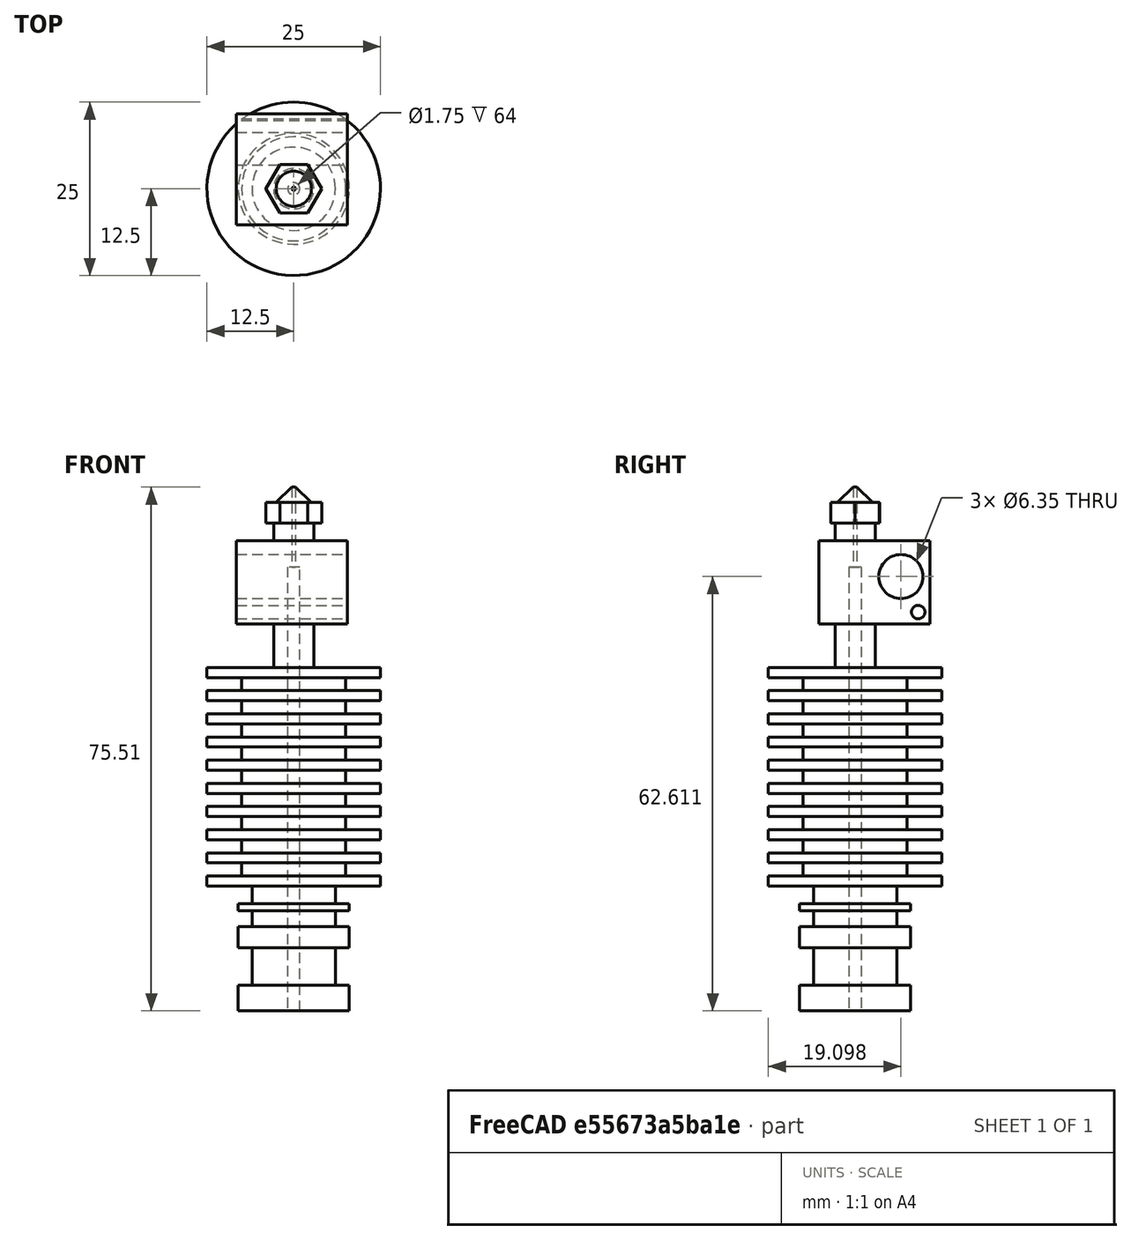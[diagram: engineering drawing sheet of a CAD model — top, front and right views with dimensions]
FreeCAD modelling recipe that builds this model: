
FCSTD DOCUMENT  (FreeCAD 0.14R3700 (Git))
Label: hotend
License: CC-BY 3.0
LicenseURL: http://creativecommons.org/licenses/by/3.0/
objects: Part::Cylinder×16, Part::Feature×3, Part::MultiFuse×3, Sketcher::SketchObject×2, PartDesign::Pocket×2, Part::Box×1, App::DocumentObjectGroup×1
note: 29 computed .brp shape members not serialized (recipe doc carries the construction recipe); baked Part::Feature solids carry a one-line shape summary decoded from their .brp

FEATURE [Part::Cylinder] Cylinder  label="Cilindro"
  Angle = 360
  Height = 3.7
  Radius = 8
FEATURE [Part::Cylinder] Cylinder001  label="Cilindro001"
  Angle = 360
  Height = 18.1
  Radius = 6
FEATURE [Part::Cylinder] Cylinder002  label="Cilindro002"
  Angle = 360
  Height = 3.06
  Placement = pos=(0,-5.16545e-06,9.1) rot=(0,0,1;0rad)
  Radius = 8
FEATURE [Part::Cylinder] Cylinder003  label="Cilindro003"
  Angle = 360
  Height = 1
  Placement = pos=(0,-5.16545e-06,14.46) rot=(0,0,1;0rad)
  Radius = 8
FEATURE [Part::Cylinder] Cylinder004  label="Cilindro004"
  Angle = 360
  Height = 1.44
  Placement = pos=(0,0,18) rot=(0,0,1;0rad)
  Radius = 12.5
FEATURE [Part::Cylinder] Cylinder005  label="Cilindro005"
  Angle = 360
  Height = 31
  Placement = pos=(0,0,18) rot=(0,0,1;0rad)
  Radius = 7.5
FEATURE [Part::Cylinder] Cylinder006  label="Cilindro006"
  Angle = 360
  Height = 1.44
  Placement = pos=(0,0,21.34) rot=(0,0,1;0rad)
  Radius = 12.5
FEATURE [Part::Cylinder] Cylinder007  label="Cilindro007"
  Angle = 360
  Height = 1.44
  Placement = pos=(0,0,24.68) rot=(0,0,1;0rad)
  Radius = 12.5
FEATURE [Part::Cylinder] Cylinder008  label="Cilindro008"
  Angle = 360
  Height = 1.44
  Placement = pos=(0,0,28.02) rot=(0,0,1;0rad)
  Radius = 12.5
FEATURE [Part::Cylinder] Cylinder009  label="Cilindro009"
  Angle = 360
  Height = 1.44
  Placement = pos=(0,0,31.36) rot=(0,0,1;0rad)
  Radius = 12.5
FEATURE [Part::Cylinder] Cylinder010  label="Cilindro010"
  Angle = 360
  Height = 1.44
  Placement = pos=(0,0,34.7) rot=(0,0,1;0rad)
  Radius = 12.5
FEATURE [Part::Cylinder] Cylinder011  label="Cilindro011"
  Angle = 360
  Height = 1.44
  Placement = pos=(0,0,38.04) rot=(0,0,1;0rad)
  Radius = 12.5
FEATURE [Part::Cylinder] Cylinder012  label="Cilindro012"
  Angle = 360
  Height = 1.44
  Placement = pos=(0,0,41.38) rot=(0,0,1;0rad)
  Radius = 12.5
FEATURE [Part::Cylinder] Cylinder013  label="Cilindro013"
  Angle = 360
  Height = 1.44
  Placement = pos=(0,0,44.72) rot=(0,0,1;0rad)
  Radius = 12.5
FEATURE [Part::Cylinder] Cylinder014  label="Cilindro014"
  Angle = 360
  Height = 1.44
  Placement = pos=(0,0,48.06) rot=(0,0,1;0rad)
  Radius = 12.5
FEATURE [Part::Cylinder] Cylinder015  label="Cilindro015"
  Angle = 360
  Height = 11.5
  Placement = pos=(0,0,48) rot=(0,0,1;0rad)
  Radius = 2.9
FEATURE [Part::Box] Box  label="Cubo"
  Height = 12
  Length = 16
  Placement = pos=(-8.26,-5.2,55.8) rot=(0,0,1;0rad)
  Width = 16
FEATURE [Sketcher::SketchObject] Sketch
  Placement = pos=(7.74,-5.2,55.8) rot=(0.57735,0.57735,0.57735;2.0944rad)
  Support = -> Box [Face2]
  sketch-geometry (2):
    g0: Circle CenterX=11.7982 CenterY=6.81083 CenterZ=0 NormalX=0 NormalY=0 NormalZ=1 Radius=3.175
    g1: Circle CenterX=14.2931 CenterY=1.69507 CenterZ=0 NormalX=0 NormalY=0 NormalZ=1 Radius=0.97
  constraints (2):
    c: Radius(g0) = 3.175
    c: Radius(g1) = 0.97
FEATURE [PartDesign::Pocket] Pocket
  Length = 5
  Placement = pos=(-8.26,-5.2,55.8) rot=(0,0,1;0rad)
  Sketch = -> Sketch
  Type = 1
FEATURE [Part::Feature] Pocket001  label="hotend-nozzle-final"
  Placement = pos=(0.0103438,0.00959258,77) rot=(1,0,0;3.14159rad)
  shape: bbox 8.08 x 7 x 11.51 mm, 19 faces (baked)
FEATURE [Part::MultiFuse] Fusion
  Shapes = -> [Cylinder,Cylinder011,Cylinder005,Cylinder009,Cylinder004,Cylinder013,Cylinder003,Cylinder008,Cylinder007,Cylinder006,Cylinder010,Cylinder002,Cylinder014,Cylinder001,Cylinder012]
FEATURE [Part::MultiFuse] Fusion001
  Shapes = -> [Pocket,Cylinder015,Fusion]
FEATURE [App::DocumentObjectGroup] Grupo
  Group = -> [Fusion001]
FEATURE [Part::Feature] Fusion001001  label="Fusion002"
  shape: bbox 25 x 25 x 67.8 mm, 60 faces (baked)
FEATURE [Sketcher::SketchObject] Sketch001
  Placement = pos=(0,0,0) rot=(1,0,0;3.14159rad)
  Support = -> Fusion001001 [Face60]
  sketch-geometry (1):
    g0: Circle CenterX=0 CenterY=0 CenterZ=0 NormalX=0 NormalY=0 NormalZ=1 Radius=0.875
  constraints (2):
    c: Coincident(g0,g-1)
    c: Radius(g0) = 0.875
FEATURE [PartDesign::Pocket] Pocket002
  Length = 5
  Sketch = -> Sketch001
  Type = 1
FEATURE [Part::MultiFuse] Fusion001002  label="Fusion003"
  Shapes = -> [Pocket002,Pocket001]
FEATURE [Part::Feature] Fusion001002001  label="hotend final001"
  shape: bbox 25 x 25 x 75.51 mm, 79 faces (baked)
